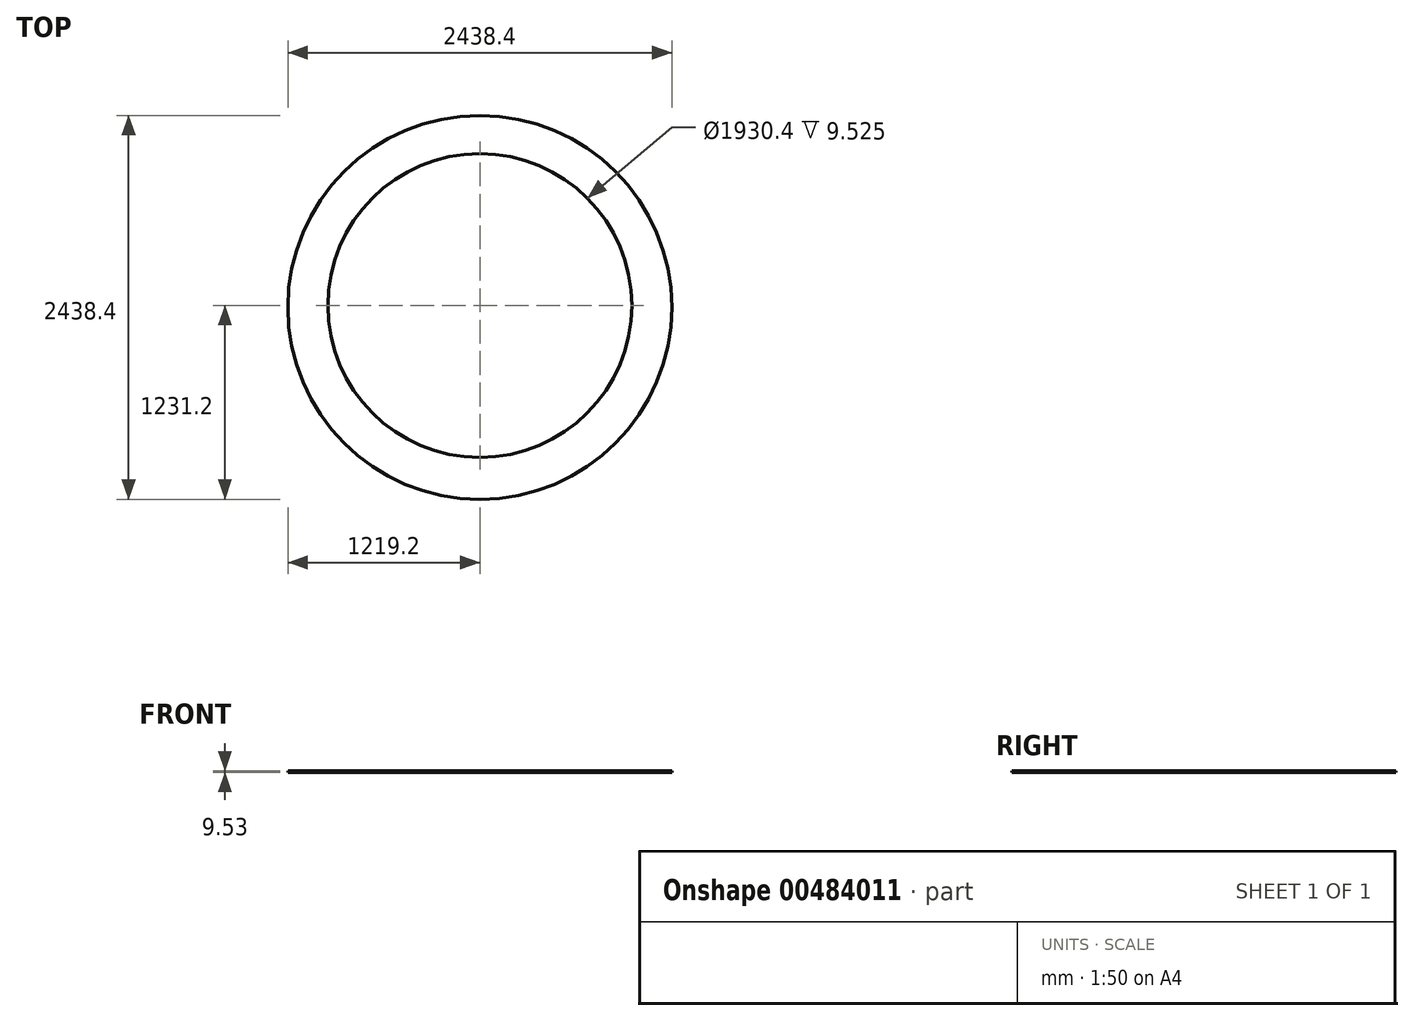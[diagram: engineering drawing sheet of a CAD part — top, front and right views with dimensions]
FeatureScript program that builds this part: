
annotation { "Feature Type Name" : "Feature", "Feature Type Description" : "" }
export const myFeature = defineFeature(function(context is Context, id is Id, definition is map)
    precondition{}
    {
        {
            var Q0;
            Q0=qCreatedBy(makeId("Top.planeOp"),FACE);
            var sketch = newSketch(context, id + "F0", { "sketchPlane" : qUnion([Q0])});
            skCircle(sketch, "E0", {"center": v(0, 0) * mm, "radius": 1219.2 * mm});
            skCircle(sketch, "E1", {"center": v(0, 12) * mm, "radius": 965.2 * mm});
            skSolve(sketch);
        }
        {
            var Q0;
            Q0=makeQuery(id+"F0.imprint","IMPRINT",FACE,{"disambiguationData":[TD([[makeQuery(id+"F0.imprint","IMPRINT",EDGE,{"derivedFrom":sQuery(id+"F0.wireOp",EDGE,"E0")}),1.0]])]});
            extrude(context, id + "F1", {"entities" : qUnion([Q0]), "depth" : 9.52 * mm});
        }
    });
